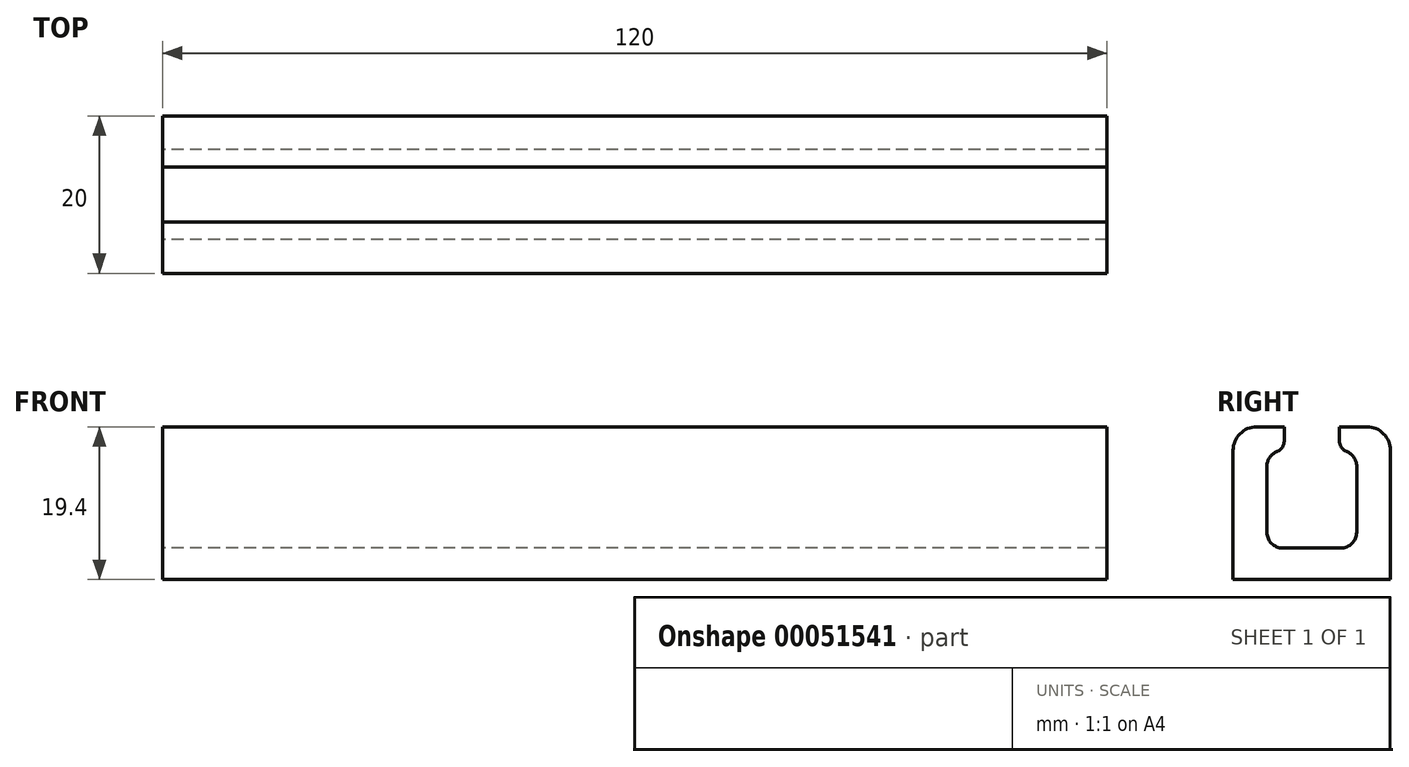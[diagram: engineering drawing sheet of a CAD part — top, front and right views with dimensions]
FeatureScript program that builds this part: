
annotation { "Feature Type Name" : "Feature", "Feature Type Description" : "" }
export const myFeature = defineFeature(function(context is Context, id is Id, definition is map)
    precondition{}
    {
        {
            var Q0;
            Q0=qCreatedBy(makeId("Right.planeOp"),FACE);
            var sketch = newSketch(context, id + "F0", { "sketchPlane" : qUnion([Q0])});
            skLineSegment(sketch, "E0", {"start": v(-10, 0) * mm, "end": v(-10, 19.4) * mm});
            skLineSegment(sketch, "E1", {"start": v(-10, 19.4) * mm, "end": v(-3.5, 19.4) * mm});
            skLineSegment(sketch, "E2", {"start": v(-5.7, 4) * mm, "end": v(0, 4) * mm});
            skLineSegment(sketch, "E3", {"start": v(0, 4) * mm, "end": v(0, 0) * mm});
            skLineSegment(sketch, "E4", {"start": v(-10, 0) * mm, "end": v(0, 0) * mm});
            skLineSegment(sketch, "E5.bottom", {"start": v(-3.5, 35.6) * mm, "end": v(3.5, 35.6) * mm, "construction": true});
            skLineSegment(sketch, "E5.top", {"start": v(-3.5, 6.2) * mm, "end": v(3.5, 6.2) * mm, "construction": true});
            skLineSegment(sketch, "E5.left", {"start": v(-3.5, 35.6) * mm, "end": v(-3.5, 6.2) * mm, "construction": true});
            skLineSegment(sketch, "E5.right", {"start": v(3.5, 35.6) * mm, "end": v(3.5, 6.2) * mm, "construction": true});
            skLineSegment(sketch, "E6", {"start": v(-3.5, 19.4) * mm, "end": v(-3.5, 16.4) * mm});
            skLineSegment(sketch, "E7", {"start": v(-3.5, 16.4) * mm, "end": v(-5.7, 16.4) * mm});
            skLineSegment(sketch, "E8", {"start": v(-5.7, 16.4) * mm, "end": v(-5.7, 4) * mm});
            skSolve(sketch);
        }
        {
            var Q0;
            Q0=makeQuery(id+"F0.imprint","IMPRINT",FACE,{"disambiguationData":[TD([[makeQuery(id+"F0.imprint","IMPRINT",EDGE,{"derivedFrom":sQuery(id+"F0.wireOp",EDGE,"E0")}),-1.0]])]});
            extrude(context, id + "F1", {"entities" : qUnion([Q0]), "depth" : 120 * mm});
        }
        {
            var Q0;
            Q0=makeQuery(id+"F1.opExtrude","SWEPT_BODY",BODY,{"disambiguationData":[OSD([sQuery(id+"F0.wireOp",EDGE,"E0"),sQuery(id+"F0.wireOp",EDGE,"E1"),sQuery(id+"F0.wireOp",EDGE,"9861b731-b71b-4ced-b63a-2fe4e3c3d2ae"),sQuery(id+"F0.wireOp",EDGE,"E2"),sQuery(id+"F0.wireOp",EDGE,"E3"),sQuery(id+"F0.wireOp",EDGE,"E4")])]});
            var Q1;
            Q1=qCreatedBy(makeId("Front.planeOp"),FACE);
            mirror(context, id + "F2", {"operationType" : NewBodyOperationType.ADD, "entities" : qUnion([Q0]), "mirrorPlane" : qUnion([Q1])});
        }
        {
            var Q0;
            Q0=makeQuery(id+"F1.opExtrude","SWEPT_EDGE",EDGE,{"disambiguationData":[OSD([sQuery(id+"F0.wireOp",EDGE,"E7"),sQuery(id+"F0.wireOp",EDGE,"E8")])]});
            var Q1;
            Q1=makeQuery(id+"F1.opExtrude","SWEPT_EDGE",EDGE,{"disambiguationData":[OSD([sQuery(id+"F0.wireOp",EDGE,"E2"),sQuery(id+"F0.wireOp",EDGE,"E8")])]});
            var Q2;
            Q2=makeQuery(id+"F2.opPattern","COPY",EDGE,{"derivedFrom":makeQuery(id+"F1.opExtrude","SWEPT_EDGE",EDGE,{"disambiguationData":[OSD([sQuery(id+"F0.wireOp",EDGE,"E2"),sQuery(id+"F0.wireOp",EDGE,"E8")])]}),"instanceName":"1"});
            var Q3;
            Q3=makeQuery(id+"F2.opPattern","COPY",EDGE,{"derivedFrom":makeQuery(id+"F1.opExtrude","SWEPT_EDGE",EDGE,{"disambiguationData":[OSD([sQuery(id+"F0.wireOp",EDGE,"E7"),sQuery(id+"F0.wireOp",EDGE,"E8")])]}),"instanceName":"1"});
            fillet(context, id + "F3", {"entities" : qUnion([Q0, Q1, Q2, Q3]), "radius" : 2 * mm, "tangentPropagation" : true, "allowEdgeOverflow" : false});
        }
        {
            var Q0;
            Q0=makeQuery(id+"F1.opExtrude","SWEPT_EDGE",EDGE,{"disambiguationData":[OSD([sQuery(id+"F0.wireOp",EDGE,"E0"),sQuery(id+"F0.wireOp",EDGE,"E1")])]});
            var Q1;
            Q1=makeQuery(id+"F2.opPattern","COPY",EDGE,{"derivedFrom":makeQuery(id+"F1.opExtrude","SWEPT_EDGE",EDGE,{"disambiguationData":[OSD([sQuery(id+"F0.wireOp",EDGE,"E0"),sQuery(id+"F0.wireOp",EDGE,"E1")])]}),"instanceName":"1"});
            fillet(context, id + "F4", {"entities" : qUnion([Q0, Q1]), "radius" : 3 * mm, "tangentPropagation" : true, "allowEdgeOverflow" : false});
        }
        {
            var Q0;
            Q0=makeQuery(id+"F1.opExtrude","SWEPT_EDGE",EDGE,{"disambiguationData":[OSD([sQuery(id+"F0.wireOp",EDGE,"E6"),sQuery(id+"F0.wireOp",EDGE,"E7")])]});
            var Q1;
            Q1=makeQuery(id+"F2.opPattern","COPY",EDGE,{"derivedFrom":makeQuery(id+"F1.opExtrude","SWEPT_EDGE",EDGE,{"disambiguationData":[OSD([sQuery(id+"F0.wireOp",EDGE,"E6"),sQuery(id+"F0.wireOp",EDGE,"E7")])]}),"instanceName":"1"});
            fillet(context, id + "F5", {"entities" : qUnion([Q0, Q1]), "radius" : 1.5 * mm, "tangentPropagation" : true, "allowEdgeOverflow" : false});
        }
    });
